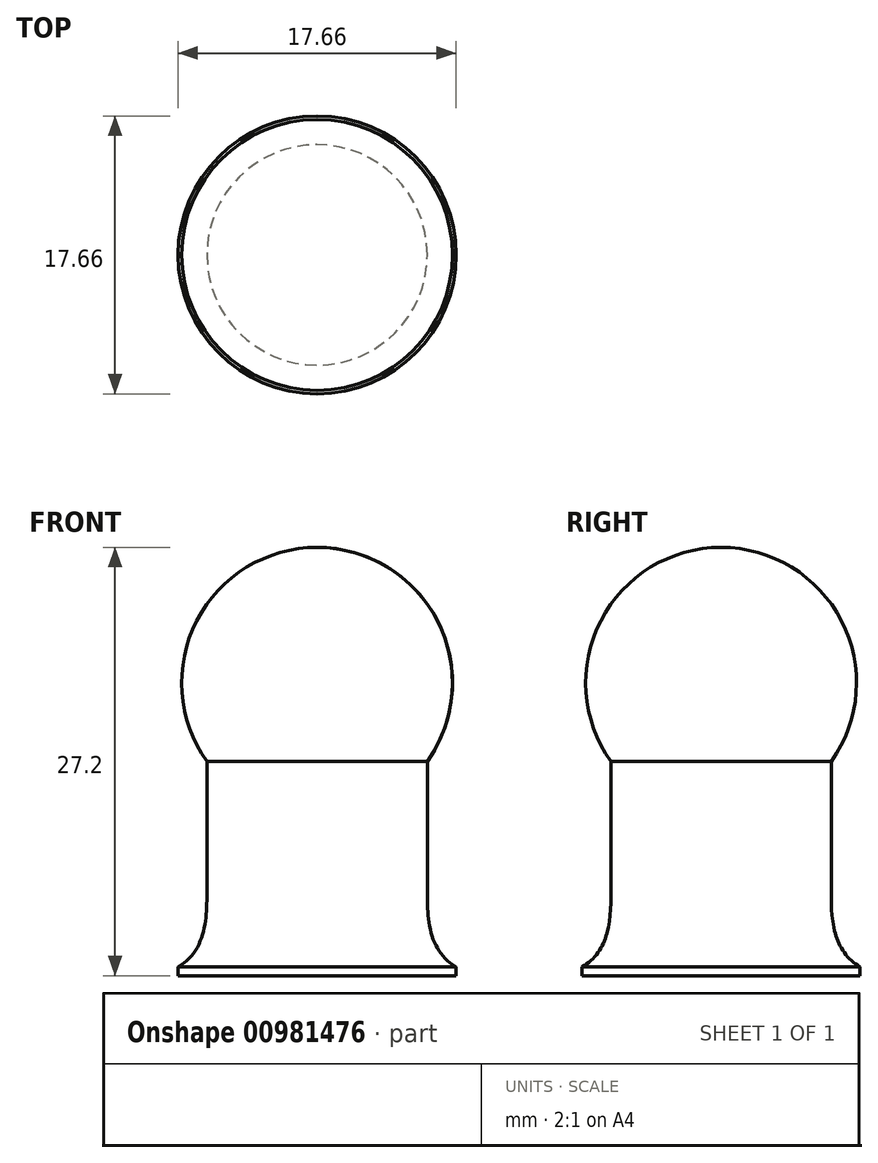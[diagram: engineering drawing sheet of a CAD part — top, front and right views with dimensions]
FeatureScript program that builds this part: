
annotation { "Feature Type Name" : "Feature", "Feature Type Description" : "" }
export const myFeature = defineFeature(function(context is Context, id is Id, definition is map)
    precondition{}
    {
        {
            var Q0;
            Q0=qCreatedBy(makeId("Front.planeOp"),FACE);
            var sketch = newSketch(context, id + "F0", { "sketchPlane" : qUnion([Q0])});
            skLineSegment(sketch, "E0.bottom", {"start": v(7, 0) * mm, "end": v(0, 0) * mm});
            skLineSegment(sketch, "E0.top", {"start": v(7, 10) * mm, "end": v(0, 10) * mm});
            skLineSegment(sketch, "E0.left", {"start": v(0, 0) * mm, "end": v(0, 10) * mm});
            skLineSegment(sketch, "E0.right", {"start": v(7, 0) * mm, "end": v(7, 10) * mm});
            skArc(sketch, "E1", {"start": v(0, 10) * mm, "mid": v(8.6, 18.6) * mm, "end": v(0, 27.2) * mm});
            skLineSegment(sketch, "E2", {"start": v(0, 27.2) * mm, "end": v(0, 10) * mm});
            skLineSegment(sketch, "E3", {"start": v(7, 10) * mm, "end": v(7, 13.6) * mm});
            skLineSegment(sketch, "E4", {"start": v(0, 0) * mm, "end": v(11.53, 0) * mm});
            skLineSegment(sketch, "E5", {"start": v(7, 0) * mm, "end": v(7, 5) * mm});
            skFitSpline(sketch, "E6", {"points": [v(7, 5) * mm, v(11.53, 0) * mm], "startDerivative": vector(0, -7.9) * mm, "endDerivative": vector(11.87, 0) * mm});
            skLineSegment(sketch, "E7", {"start": v(8.83, 0.57) * mm, "end": v(8.83, 0) * mm});
            skSolve(sketch);
        }
        {
            var Q0;
            {var subQ0=sQuery(id+"F0.wireOp",EDGE,"E2");Q0=makeQuery(id+"F0.imprint","IMPRINT",FACE,{"disambiguationData":[TD([[makeQuery(id+"F0.imprint","IMPRINT",EDGE,{"derivedFrom":subQ0}),1.0]])]});}
            var Q1;
            {var subQ0=sQuery(id+"F0.wireOp",EDGE,"E0.top");Q1=makeQuery(id+"F0.imprint","IMPRINT",FACE,{"disambiguationData":[TD([[makeQuery(id+"F0.imprint","IMPRINT",EDGE,{"derivedFrom":subQ0}),-1.0]])]});}
            var Q2;
            Q2=makeQuery(id+"F0.imprint","IMPRINT",FACE,{"disambiguationData":[TD([[makeQuery(id+"F0.imprint","IMPRINT",EDGE,{"derivedFrom":sQuery(id+"F0.wireOp",EDGE,"E0.bottom")}),-1.0]])]});
            var Q3;
            {var subQ1=sQuery(id+"F0.wireOp",EDGE,"E0.bottom");Q3=makeQuery(id+"F0.imprint","IMPRINT",FACE,{"disambiguationData":[TD([[makeQuery(id+"F0.imprint","IMPRINT",EDGE,{"derivedFrom":subQ1}),-1.0]])]});}
            var Q4;
            {var subQ5=sQuery(id+"F0.wireOp",EDGE,"E7");Q4=makeQuery(id+"F0.imprint","IMPRINT",FACE,{"disambiguationData":[TD([[makeQuery(id+"F0.imprint","IMPRINT",EDGE,{"derivedFrom":subQ5}),-1.0]])]});}
            var Q5;
            Q5=sQuery(id+"F0.wireOp",EDGE,"E2");
            revolve(context, id + "F1", {"surfaceOperationType" : NewSurfaceOperationType.NEW, "entities" : qUnion([Q0, Q1, Q2, Q3, Q4]), "axis" : qUnion([Q5]), "revolveType" : RevolveType.FULL});
        }
    });
